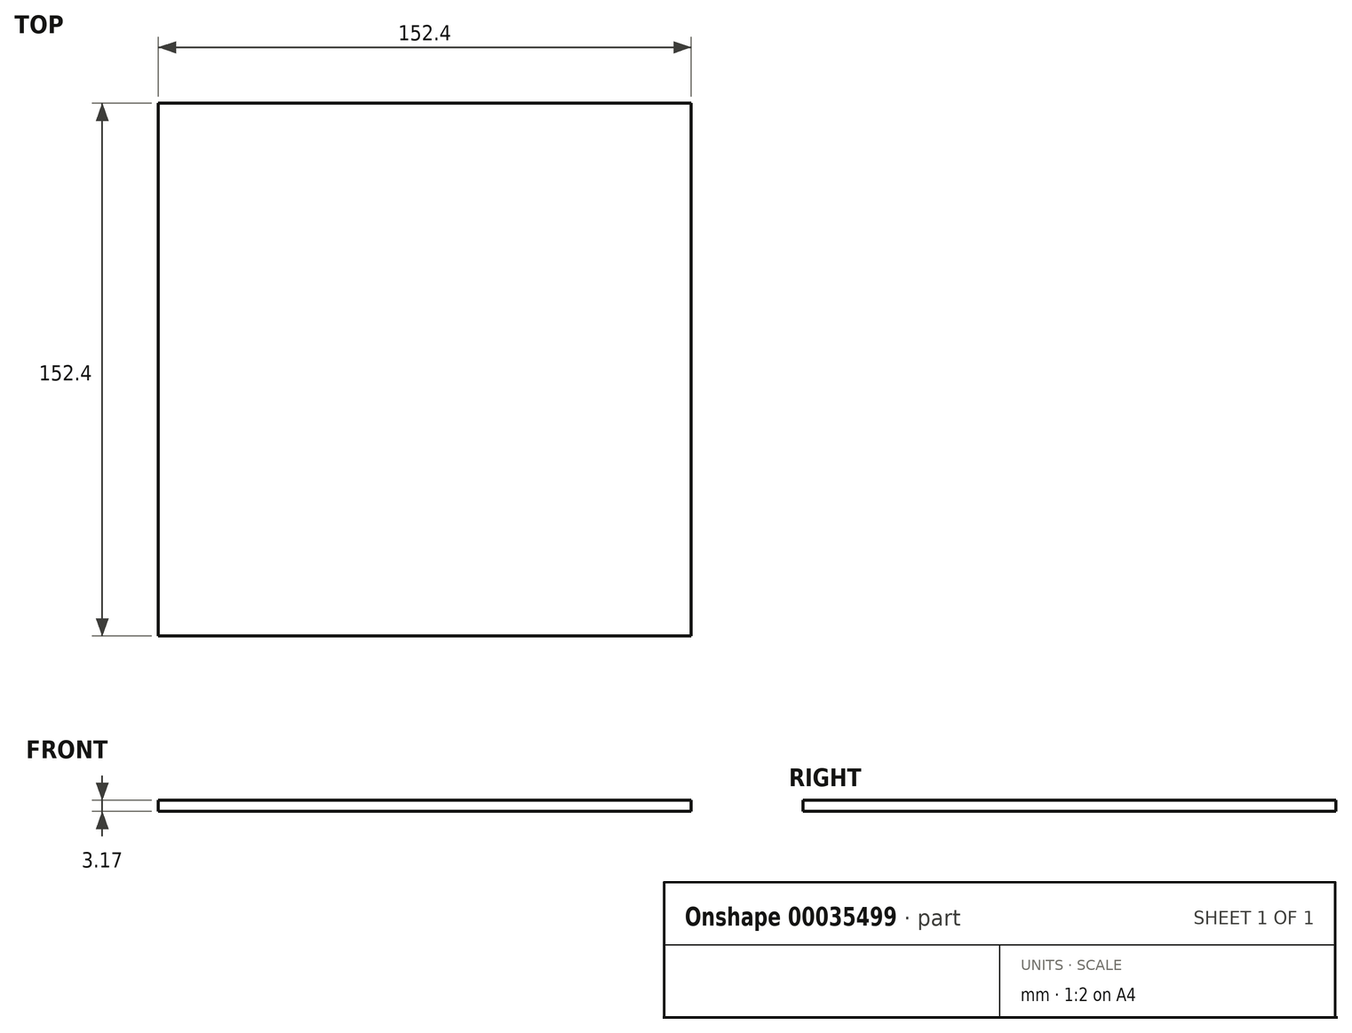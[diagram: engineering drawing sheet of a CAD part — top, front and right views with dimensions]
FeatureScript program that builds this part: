
annotation { "Feature Type Name" : "Feature", "Feature Type Description" : "" }
export const myFeature = defineFeature(function(context is Context, id is Id, definition is map)
    precondition{}
    {
        {
            var Q0;
            Q0=qCreatedBy(makeId("Top.planeOp"),FACE);
            var sketch = newSketch(context, id + "F0", { "sketchPlane" : qUnion([Q0])});
            skLineSegment(sketch, "E0.rect.bottom", {"start": v(76.2, 76.2) * mm, "end": v(-76.2, 76.2) * mm});
            skLineSegment(sketch, "E0.rect.top", {"start": v(76.2, -76.2) * mm, "end": v(-76.2, -76.2) * mm});
            skLineSegment(sketch, "E0.rect.left", {"start": v(76.2, 76.2) * mm, "end": v(76.2, -76.2) * mm});
            skLineSegment(sketch, "E0.rect.right", {"start": v(-76.2, 76.2) * mm, "end": v(-76.2, -76.2) * mm});
            skPoint(sketch, "E0.rect.middle", {"position": v(0, 0) * mm});
            skSolve(sketch);
        }
        {
            var Q0;
            Q0=makeQuery(id+"F0.imprint","IMPRINT",FACE,{"disambiguationData":[TD([[makeQuery(id+"F0.imprint","IMPRINT",EDGE,{"derivedFrom":sQuery(id+"F0.wireOp",EDGE,"E0.rect.bottom")}),1.0]])]});
            extrude(context, id + "F1", {"entities" : qUnion([Q0]), "depth" : 3.17 * mm});
        }
    });
